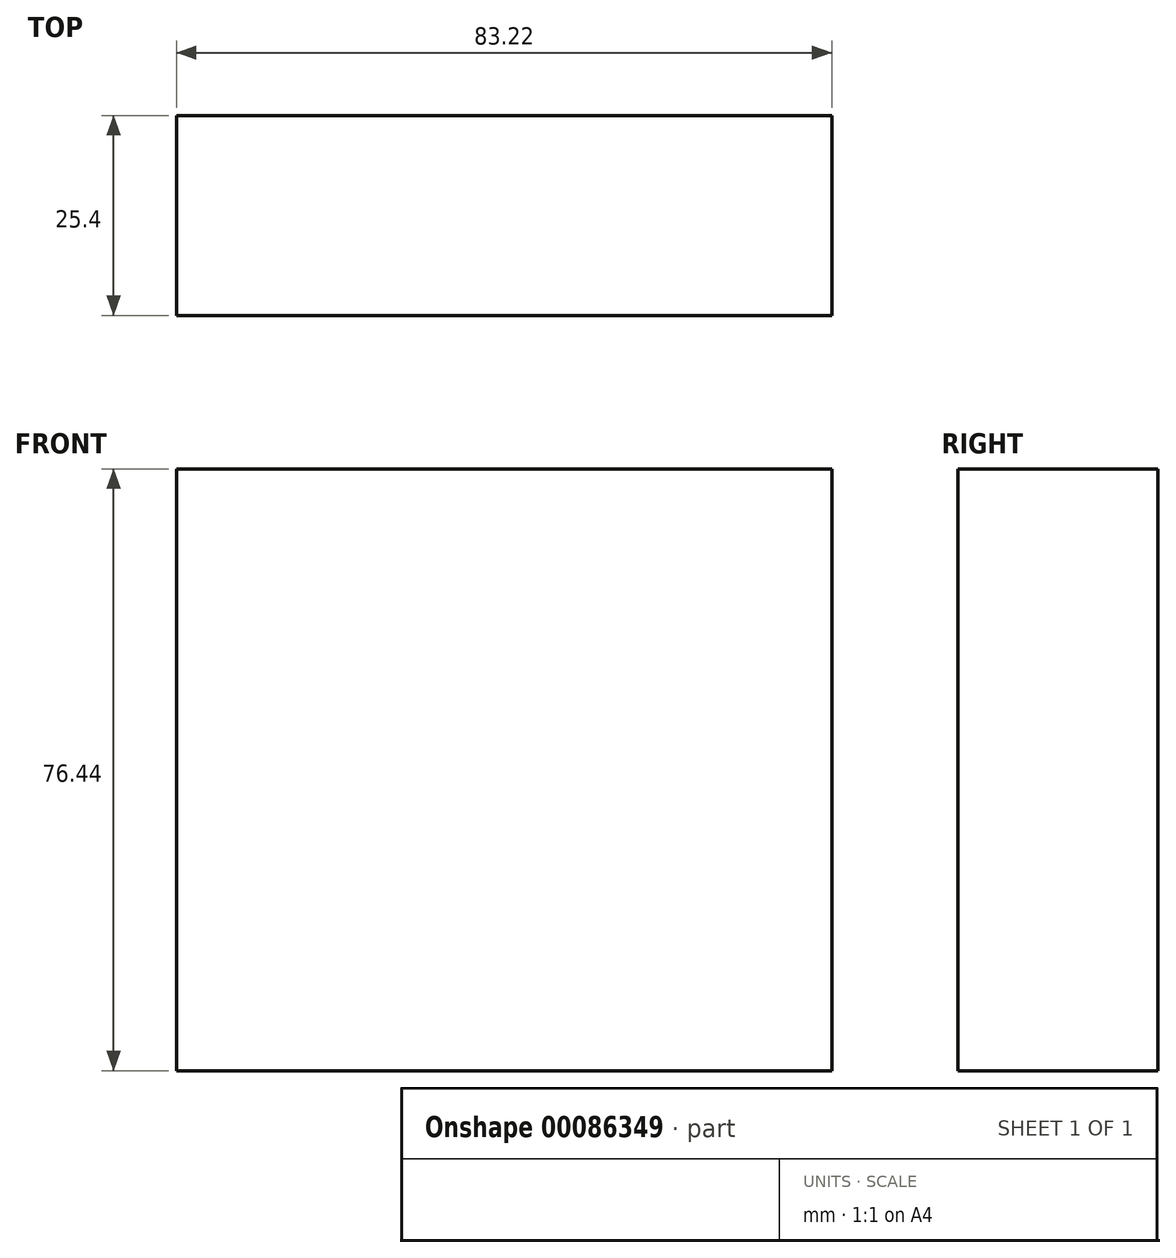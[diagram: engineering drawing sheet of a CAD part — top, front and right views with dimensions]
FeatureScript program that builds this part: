
annotation { "Feature Type Name" : "Feature", "Feature Type Description" : "" }
export const myFeature = defineFeature(function(context is Context, id is Id, definition is map)
    precondition{}
    {
        {
            var Q0;
            Q0=qCreatedBy(makeId("Front.planeOp"),FACE);
            var sketch = newSketch(context, id + "F0", { "sketchPlane" : qUnion([Q0])});
            skLineSegment(sketch, "E0.bottom", {"start": v(41.6, 38.22) * mm, "end": v(-41.6, 38.22) * mm});
            skLineSegment(sketch, "E0.top", {"start": v(41.6, -38.22) * mm, "end": v(-41.6, -38.22) * mm});
            skLineSegment(sketch, "E0.left", {"start": v(41.6, 38.22) * mm, "end": v(41.6, -38.22) * mm});
            skLineSegment(sketch, "E0.right", {"start": v(-41.6, 38.22) * mm, "end": v(-41.6, -38.22) * mm});
            skPoint(sketch, "E0.middle", {"position": v(0, 0) * mm});
            skSolve(sketch);
        }
        {
            var Q0;
            Q0 = qSketchRegion(id + "F0", true);
            extrude(context, id + "F1", {"entities" : qUnion([Q0]), "depth" : 25.4 * mm});
        }
    });
